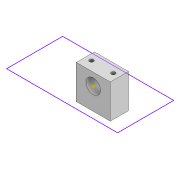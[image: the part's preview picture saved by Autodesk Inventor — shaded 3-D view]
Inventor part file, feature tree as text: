
AUTODESK INVENTOR PART (.ipt)
format: ipt  version: 2022 (Build 260153000, 153)  size: 113,152 bytes
history: native  units: mm
features: sketch x4, extrude x3
ambient origin geometry x8: Origin, YZ Plane, XZ Plane, XY Plane, X Axis, Y Axis, Z Axis, Center Point
bodies: Solid1 (feature_tree)
feature tree (7):
  extrude  "Extrusion1"  Depth=10.0mm
  extrude  "Extrusion2"  Depth=14.0mm
  extrude  "Extrusion3"  Depth=15.0mm TaperAngle=0.0deg
  sketch  "Sketch4"  dims[d7=8.2mm d8=14.0mm d9=7.5mm d10=10.0mm d11=0.0mm d12=3.2mm d13=3.2mm d14=5.0mm d15=5.0mm d16=7.5mm d17=7.5mm d18=100.0mm d19=0.0mm]
  sketch  "Sketch1"  dims[d0=11.9mm d1=10.0mm]
  sketch  "Sketch2"  dims[d2=14.0mm d3=14.0mm]
  sketch  "Sketch3"  dims[d4=18.0mm d5=15.0mm d6=0.0mm]
